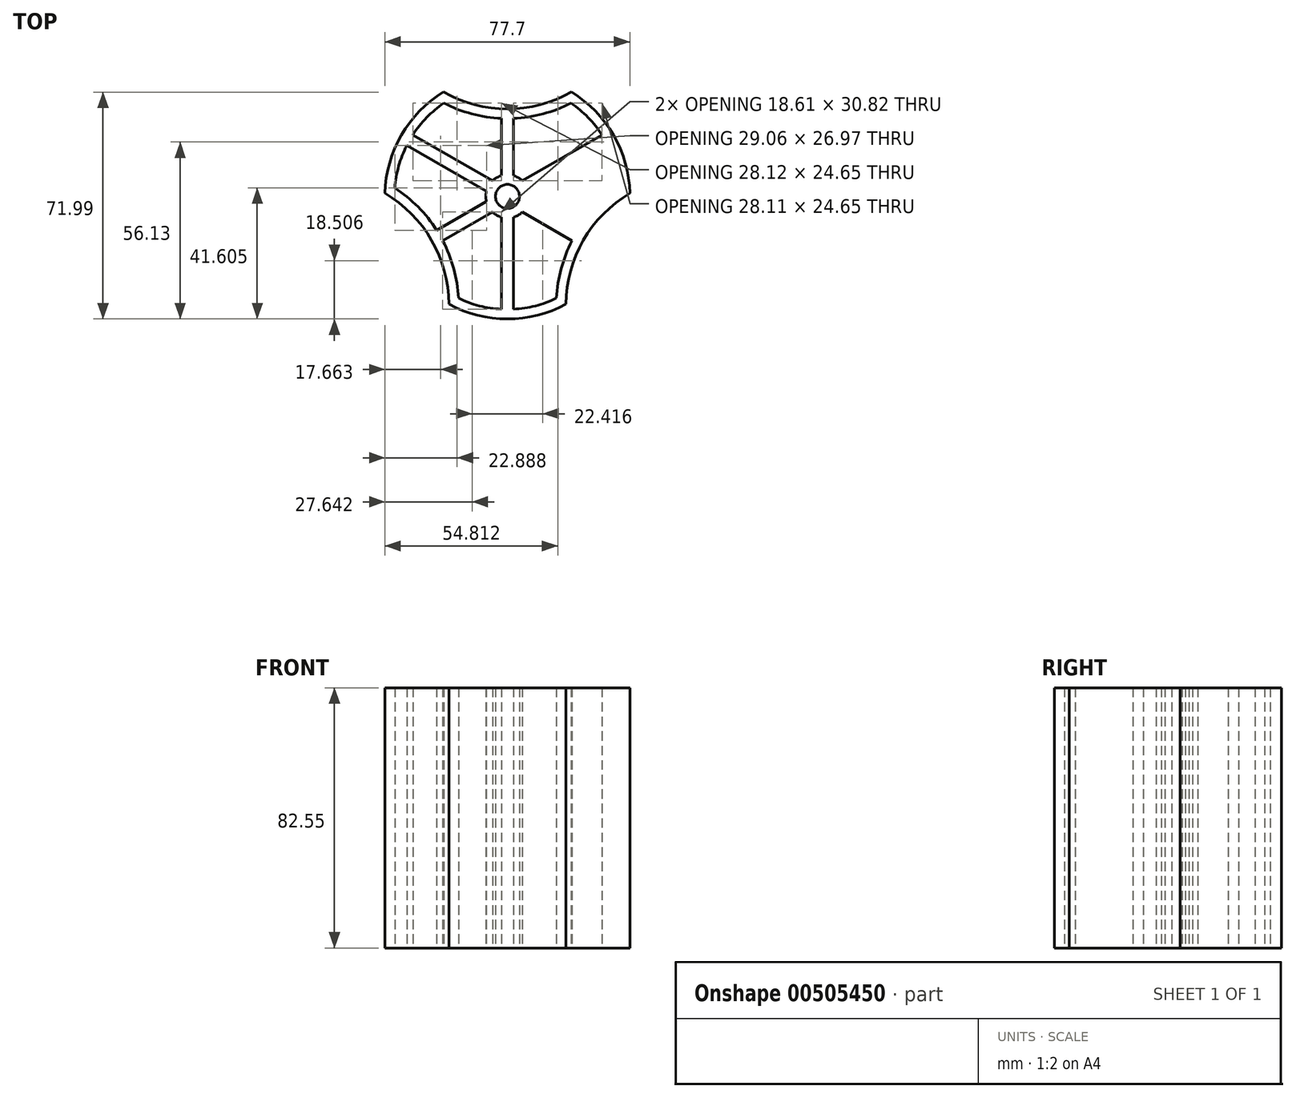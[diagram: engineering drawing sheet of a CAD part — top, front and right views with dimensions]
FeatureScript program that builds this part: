
annotation { "Feature Type Name" : "Feature", "Feature Type Description" : "" }
export const myFeature = defineFeature(function(context is Context, id is Id, definition is map)
    precondition{}
    {
        {
            var Q0;
            Q0=qCreatedBy(makeId("Top.planeOp"),FACE);
            var sketch = newSketch(context, id + "F0", { "sketchPlane" : qUnion([Q0])});
            skCircle(sketch, "E0", {"center": v(0, 0) * mm, "radius": 3.81 * mm});
            skArc(sketch, "E1", {"start": v(-20.3, 33.13) * mm, "mid": v(-33.66, 19.43) * mm, "end": v(-38.85, 1.02) * mm});
            skArc(sketch, "E2", {"start": v(-20.3, 33.13) * mm, "mid": v(0, 27.8) * mm, "end": v(20.3, 33.13) * mm});
            skArc(sketch, "E3.1.0", {"start": v(-18.54, -34.15) * mm, "mid": v(-24.07, -13.9) * mm, "end": v(-38.85, 1.02) * mm});
            skArc(sketch, "E3.2.0", {"start": v(38.85, 1.02) * mm, "mid": v(24.07, -13.9) * mm, "end": v(18.54, -34.15) * mm});
            skArc(sketch, "E4.trimOffspring", {"start": v(-18.54, -34.15) * mm, "mid": v(0, -38.86) * mm, "end": v(18.54, -34.15) * mm});
            skArc(sketch, "E5.trimOffspring", {"start": v(38.85, 1.02) * mm, "mid": v(33.66, 19.43) * mm, "end": v(20.3, 33.13) * mm});
            skPoint(sketch, "E6.center.orphan", {"position": v(-33.66, 19.43) * mm});
            skPoint(sketch, "E7.center.orphan", {"position": v(-37.85, 8.8) * mm});
            skPoint(sketch, "E8.center.orphan", {"position": v(-26.55, 28.38) * mm});
            skLineSegment(sketch, "E9", {"start": v(-31.92, 16.23) * mm, "end": v(-3.8, 0) * mm});
            skLineSegment(sketch, "E10", {"start": v(-30.02, 19.53) * mm, "end": v(-4.75, 4.94) * mm});
            skArc(sketch, "E11.0", {"start": v(-20.17, 29.6) * mm, "mid": v(-25.6, 25.05) * mm, "end": v(-30.02, 19.53) * mm});
            skArc(sketch, "E11.1", {"start": v(35.71, 2.67) * mm, "mid": v(34.5, 9.64) * mm, "end": v(31.92, 16.23) * mm});
            skArc(sketch, "E11.2", {"start": v(35.71, 2.67) * mm, "mid": v(28.34, -3.32) * mm, "end": v(22.42, -10.74) * mm});
            skArc(sketch, "E11.3", {"start": v(-20.17, 29.6) * mm, "mid": v(-11.3, 26.2) * mm, "end": v(-1.9, 24.78) * mm});
            skArc(sketch, "E11.4", {"start": v(-15.55, -32.26) * mm, "mid": v(-8.9, -34.7) * mm, "end": v(-1.9, -35.76) * mm});
            skArc(sketch, "E11.5", {"start": v(-15.55, -32.26) * mm, "mid": v(-17.05, -22.88) * mm, "end": v(-20.51, -14.04) * mm});
            skLineSegment(sketch, "E12.1.0", {"start": v(-1.9, -35.76) * mm, "end": v(-1.9, -6.59) * mm});
            skLineSegment(sketch, "E12.1.1", {"start": v(1.9, -35.76) * mm, "end": v(1.9, -6.59) * mm});
            skLineSegment(sketch, "E12.2.0", {"start": v(31.92, 16.23) * mm, "end": v(6.66, 1.65) * mm});
            skLineSegment(sketch, "E12.2.1", {"start": v(30.02, 19.53) * mm, "end": v(4.75, 4.94) * mm});
            skArc(sketch, "E13.0", {"start": v(1.9, -6.59) * mm, "mid": v(3.43, -5.94) * mm, "end": v(4.75, -4.94) * mm});
            skLineSegment(sketch, "E14", {"start": v(-1.9, 24.78) * mm, "end": v(-1.9, 6.59) * mm});
            skLineSegment(sketch, "E15", {"start": v(1.9, 24.78) * mm, "end": v(1.9, 6.59) * mm});
            skLineSegment(sketch, "E16.1.0", {"start": v(-20.51, -14.04) * mm, "end": v(-4.75, -4.94) * mm});
            skLineSegment(sketch, "E16.1.1", {"start": v(-22.42, -10.74) * mm, "end": v(-6.66, -1.64) * mm});
            skLineSegment(sketch, "E16.2.0", {"start": v(22.42, -10.74) * mm, "end": v(6.66, -1.65) * mm});
            skLineSegment(sketch, "E16.2.1", {"start": v(20.51, -14.04) * mm, "end": v(4.75, -4.95) * mm});
            skPoint(sketch, "E17.orphan", {"position": v(-32.66, 21.06) * mm});
            skPoint(sketch, "E18.orphan", {"position": v(-34.57, 17.76) * mm});
            skArc(sketch, "E19.trimOffspring", {"start": v(20.51, -14.04) * mm, "mid": v(17.05, -22.89) * mm, "end": v(15.55, -32.26) * mm});
            skArc(sketch, "E20.trimOffspring", {"start": v(30.02, 19.53) * mm, "mid": v(25.6, 25.05) * mm, "end": v(20.17, 29.6) * mm});
            skArc(sketch, "E21.trimOffspring", {"start": v(1.9, 24.78) * mm, "mid": v(11.3, 26.2) * mm, "end": v(20.17, 29.6) * mm});
            skArc(sketch, "E22.trimOffspring", {"start": v(-31.92, 16.23) * mm, "mid": v(-34.5, 9.64) * mm, "end": v(-35.71, 2.67) * mm});
            skArc(sketch, "E23.trimOffspring", {"start": v(-22.42, -10.74) * mm, "mid": v(-28.34, -3.32) * mm, "end": v(-35.71, 2.67) * mm});
            skPoint(sketch, "E24.orphan", {"position": v(1.9, -38.81) * mm});
            skPoint(sketch, "E25.orphan", {"position": v(-1.9, -38.81) * mm});
            skArc(sketch, "E26.trimOffspring", {"start": v(1.9, -35.76) * mm, "mid": v(8.9, -34.7) * mm, "end": v(15.55, -32.26) * mm});
            skPoint(sketch, "E27.orphan", {"position": v(-1.9, 3.3) * mm});
            skArc(sketch, "E28.trimOffspring", {"start": v(-1.9, 6.59) * mm, "mid": v(-3.43, 5.94) * mm, "end": v(-4.75, 4.94) * mm});
            skArc(sketch, "E29.trimOffspring", {"start": v(-6.66, 1.64) * mm, "mid": v(-6.86, 0) * mm, "end": v(-6.66, -1.64) * mm});
            skArc(sketch, "E30.trimOffspring", {"start": v(6.66, -1.65) * mm, "mid": v(6.86, 0) * mm, "end": v(6.66, 1.65) * mm});
            skArc(sketch, "E31.trimOffspring", {"start": v(4.75, 4.94) * mm, "mid": v(3.43, 5.94) * mm, "end": v(1.9, 6.59) * mm});
            skPoint(sketch, "E32.orphan", {"position": v(1.9, -3.3) * mm});
            skPoint(sketch, "E33.orphan", {"position": v(-1.9, -3.3) * mm});
            skPoint(sketch, "E34.orphan", {"position": v(1.9, 3.3) * mm});
            skPoint(sketch, "E35.orphan", {"position": v(3.8, 0) * mm});
            skArc(sketch, "E36", {"start": v(-4.75, -4.94) * mm, "mid": v(-3.43, -5.94) * mm, "end": v(-1.9, -6.59) * mm});
            skArc(sketch, "E37.trimOffspring", {"start": v(1.9, -6.59) * mm, "mid": v(3.43, -5.94) * mm, "end": v(4.75, -4.95) * mm});
            skPoint(sketch, "E38.orphan", {"position": v(32.66, 21.06) * mm});
            skPoint(sketch, "E39.orphan", {"position": v(34.57, 17.76) * mm});
            skSolve(sketch);
        }
        {
            var Q0;
            Q0=qSketchRegion(id+"F0",true);
            extrude(context, id + "F1", {"entities" : qUnion([Q0]), "depth" : 82.55 * mm});
        }
    });
